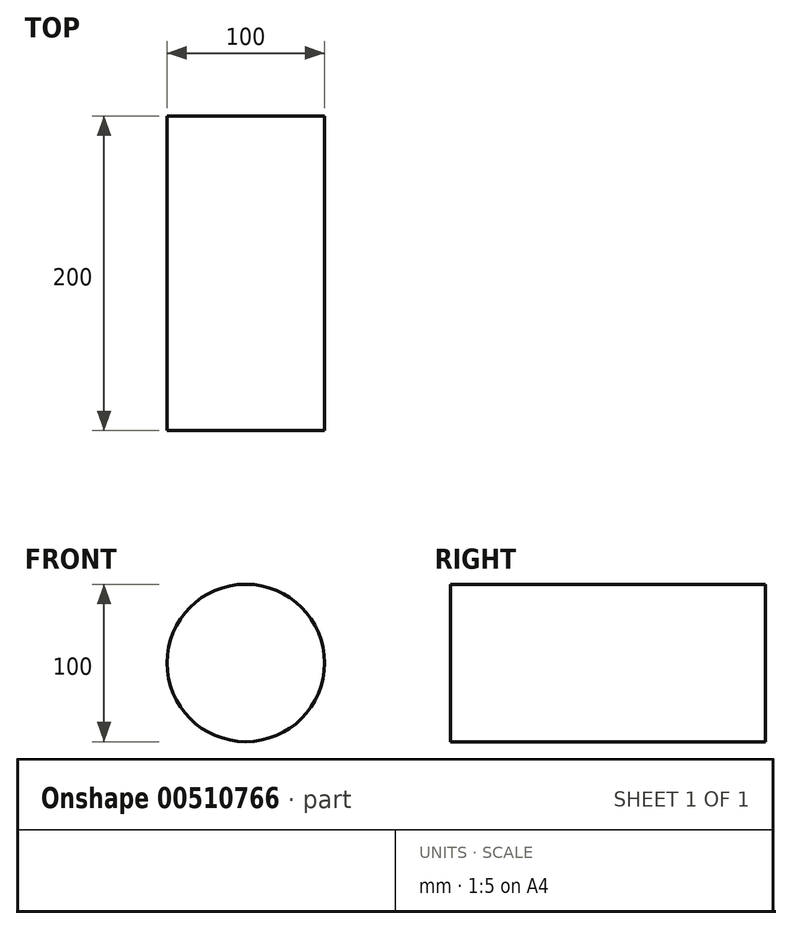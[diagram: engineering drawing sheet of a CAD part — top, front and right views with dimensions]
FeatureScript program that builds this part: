
annotation { "Feature Type Name" : "Feature", "Feature Type Description" : "" }
export const myFeature = defineFeature(function(context is Context, id is Id, definition is map)
    precondition{}
    {
        {
            var Q0;
            Q0=qCreatedBy(makeId("Front.planeOp"),FACE);
            var sketch = newSketch(context, id + "F0", { "sketchPlane" : qUnion([Q0])});
            skCircle(sketch, "E0", {"center": v(0, 0) * mm, "radius": 50 * mm});
            skSolve(sketch);
        }
        {
            var Q0;
            Q0=makeQuery(id+"F0.imprint","IMPRINT",FACE,{"disambiguationData":[TD([[makeQuery(id+"F0.imprint","IMPRINT",EDGE,{"derivedFrom":sQuery(id+"F0.wireOp",EDGE,"E0")}),1.0]])]});
            extrude(context, id + "F1", {"entities" : qUnion([Q0]), "endBound" : BoundingType.SYMMETRIC, "depth" : 200 * mm, "offsetDistance" : 25 * mm});
        }
    });
